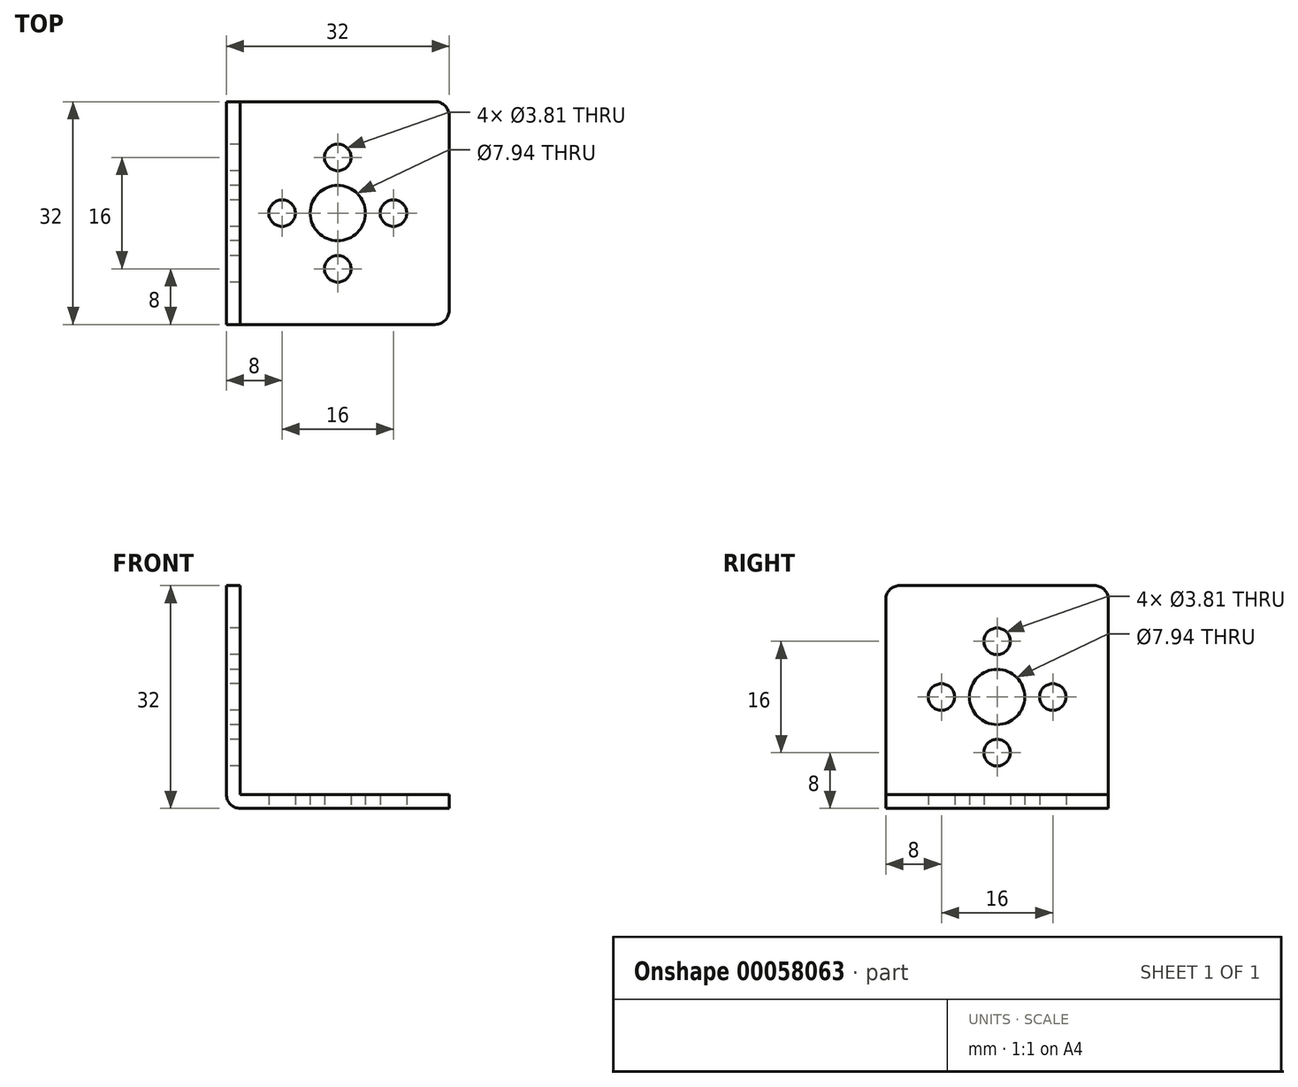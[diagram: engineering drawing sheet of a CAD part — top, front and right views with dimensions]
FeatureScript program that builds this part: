
annotation { "Feature Type Name" : "Feature", "Feature Type Description" : "" }
export const myFeature = defineFeature(function(context is Context, id is Id, definition is map)
    precondition{}
    {
        {
            var Q0;
            Q0=qCreatedBy(makeId("Top.planeOp"),FACE);
            var sketch = newSketch(context, id + "F0", { "sketchPlane" : qUnion([Q0])});
            skLineSegment(sketch, "E0.bottom", {"start": v(0, 0) * mm, "end": v(-32, 0) * mm});
            skLineSegment(sketch, "E0.top", {"start": v(0, 32) * mm, "end": v(-32, 32) * mm});
            skLineSegment(sketch, "E0.left", {"start": v(0, 0) * mm, "end": v(0, 32) * mm});
            skLineSegment(sketch, "E0.right", {"start": v(-32, 0) * mm, "end": v(-32, 32) * mm});
            skCircle(sketch, "E1", {"center": v(-16, 16) * mm, "radius": 3.97 * mm});
            skPoint(sketch, "E1.centerSnap0", {"position": v(0, 16) * mm});
            skPoint(sketch, "E1.centerSnap1", {"position": v(-16, 32) * mm});
            skCircle(sketch, "E2", {"center": v(-16, 24) * mm, "radius": 1.9 * mm});
            skCircle(sketch, "E3.1.0", {"center": v(-24, 16) * mm, "radius": 1.9 * mm});
            skCircle(sketch, "E3.2.0", {"center": v(-16, 8) * mm, "radius": 1.9 * mm});
            skCircle(sketch, "E3.3.0", {"center": v(-8, 16) * mm, "radius": 1.9 * mm});
            skSolve(sketch);
        }
        {
            var Q0;
            Q0=makeQuery(id+"F0.imprint","IMPRINT",FACE,{"disambiguationData":[TD([[makeQuery(id+"F0.imprint","IMPRINT",EDGE,{"derivedFrom":sQuery(id+"F0.wireOp",EDGE,"1bb81507-4f5c-4394-839c-011548c47b70.bottom")}),1.0]])]});
            var Q1;
            Q1=makeQuery(id+"F0.imprint","IMPRINT",FACE,{"disambiguationData":[TD([[makeQuery(id+"F0.imprint","IMPRINT",EDGE,{"derivedFrom":sQuery(id+"F0.wireOp",EDGE,"E0.bottom")}),-1.0]])]});
            extrude(context, id + "F1", {"entities" : qUnion([Q0, Q1]), "depth" : 2 * mm});
        }
        {
            var Q0;
            Q0=makeQuery(id+"F1.opExtrude","CAP_FACE",FACE,{"disambiguationData":[OSD([sQuery(id+"F0.wireOp",EDGE,"E0.bottom"),sQuery(id+"F0.wireOp",EDGE,"E0.top"),sQuery(id+"F0.wireOp",EDGE,"E0.left"),sQuery(id+"F0.wireOp",EDGE,"E0.right"),sQuery(id+"F0.wireOp",EDGE,"E1"),sQuery(id+"F0.wireOp",EDGE,"E2"),sQuery(id+"F0.wireOp",EDGE,"E3.1.0"),sQuery(id+"F0.wireOp",EDGE,"E3.2.0"),sQuery(id+"F0.wireOp",EDGE,"E3.3.0")])],"isStart":false});
            var sketch = newSketch(context, id + "F2", { "sketchPlane" : qUnion([Q0])});
            skLineSegment(sketch, "E4.bottom", {"start": v(-32, 0) * mm, "end": v(-30, 0) * mm});
            skLineSegment(sketch, "E4.top", {"start": v(-32, 32) * mm, "end": v(-30, 32) * mm});
            skLineSegment(sketch, "E4.left", {"start": v(-32, 0) * mm, "end": v(-32, 32) * mm});
            skLineSegment(sketch, "E4.right", {"start": v(-30, 0) * mm, "end": v(-30, 32) * mm});
            skSolve(sketch);
        }
        {
            var Q0;
            Q0=makeQuery(id+"F2.imprint","IMPRINT",FACE,{"disambiguationData":[TD([[makeQuery(id+"F2.imprint","IMPRINT",EDGE,{"derivedFrom":sQuery(id+"F2.wireOp",EDGE,"E4.bottom")}),-1.0]])]});
            extrude(context, id + "F3", {"entities" : qUnion([Q0]), "operationType" : NewBodyOperationType.ADD, "depth" : 30 * mm});
        }
        {
            var Q0;
            Q0=makeQuery(id+"F3.boolean.opBoolean","MERGE",FACE,{"derivedFrom":[makeQuery(id+"F1.opExtrude","SWEPT_FACE",FACE,{"disambiguationData":[OSD([sQuery(id+"F0.wireOp",EDGE,"E0.right")])]}),makeQuery(id+"F3.opExtrude","SWEPT_FACE",FACE,{"disambiguationData":[OSD([sQuery(id+"F2.wireOp",EDGE,"E4.left")])]})]});
            var sketch = newSketch(context, id + "F4", { "sketchPlane" : qUnion([Q0])});
            skCircle(sketch, "E5", {"center": v(-16, 16) * mm, "radius": 3.97 * mm});
            skPoint(sketch, "E5.centerSnap0", {"position": v(0, 16) * mm});
            skPoint(sketch, "E5.centerSnap1", {"position": v(-16, 32) * mm});
            skCircle(sketch, "E6", {"center": v(-16, 24) * mm, "radius": 1.9 * mm});
            skCircle(sketch, "E7.1.0", {"center": v(-24, 16) * mm, "radius": 1.9 * mm});
            skCircle(sketch, "E7.2.0", {"center": v(-16, 8) * mm, "radius": 1.9 * mm});
            skCircle(sketch, "E7.3.0", {"center": v(-8, 16) * mm, "radius": 1.9 * mm});
            skSolve(sketch);
        }
        {
            var Q0;
            Q0 = qSketchRegion(id + "F4", true);
            extrude(context, id + "F5", {"entities" : qUnion([Q0]), "operationType" : NewBodyOperationType.REMOVE, "endBound" : BoundingType.UP_TO_NEXT, "oppositeDirection" : true, "depth" : 25.4 * mm});
        }
        {
            var Q0;
            Q0=makeQuery(id+"F3.opExtrude","CAP_EDGE",EDGE,{"disambiguationData":[OSD([sQuery(id+"F2.wireOp",EDGE,"E4.bottom")])],"isStart":false});
            var Q1;
            Q1=makeQuery(id+"F3.opExtrude","CAP_EDGE",EDGE,{"disambiguationData":[OSD([sQuery(id+"F2.wireOp",EDGE,"E4.top")])],"isStart":false});
            var Q2;
            Q2=makeQuery(id+"F1.opExtrude","SWEPT_EDGE",EDGE,{"disambiguationData":[OSD([sQuery(id+"F0.wireOp",EDGE,"E0.bottom"),sQuery(id+"F0.wireOp",EDGE,"E0.left")])]});
            var Q3;
            Q3=makeQuery(id+"F1.opExtrude","SWEPT_EDGE",EDGE,{"disambiguationData":[OSD([sQuery(id+"F0.wireOp",EDGE,"E0.top"),sQuery(id+"F0.wireOp",EDGE,"E0.left")])]});
            var Q4;
            Q4=makeQuery(id+"F3.opExtrude","CAP_EDGE",EDGE,{"disambiguationData":[OSD([sQuery(id+"F2.wireOp",EDGE,"E4.right")])],"isStart":true});
            var Q5;
            Q5=makeQuery(id+"F1.opExtrude","CAP_EDGE",EDGE,{"disambiguationData":[OSD([sQuery(id+"F0.wireOp",EDGE,"E0.right")])],"isStart":true});
            fillet(context, id + "F6", {"entities" : qUnion([Q0, Q1, Q2, Q3, Q4, Q5]), "radius" : 2 * mm, "tangentPropagation" : true, "allowEdgeOverflow" : false});
        }
    });
